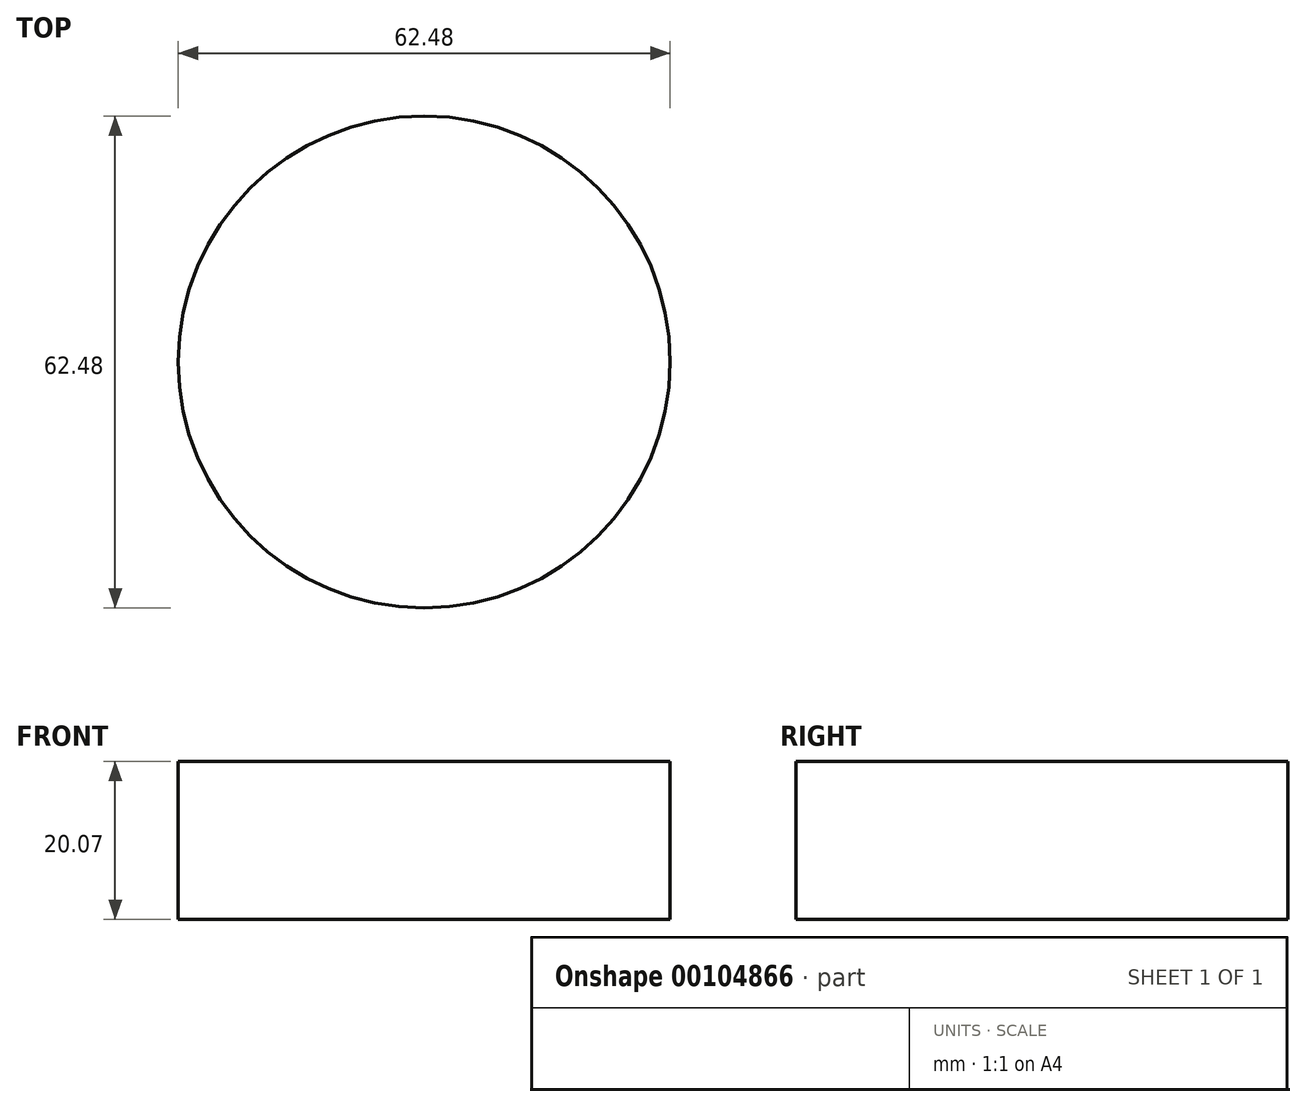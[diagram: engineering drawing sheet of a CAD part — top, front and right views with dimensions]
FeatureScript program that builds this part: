
annotation { "Feature Type Name" : "Feature", "Feature Type Description" : "" }
export const myFeature = defineFeature(function(context is Context, id is Id, definition is map)
    precondition{}
    {
        {
            var Q0;
            Q0=qCreatedBy(makeId("Top.planeOp"),FACE);
            var sketch = newSketch(context, id + "F0", { "sketchPlane" : qUnion([Q0])});
            skCircle(sketch, "E0", {"center": v(0, 0) * mm, "radius": 31.24 * mm});
            skCircle(sketch, "E1", {"center": v(0, 0) * mm, "radius": 21.46 * mm});
            skSolve(sketch);
        }
        {
            var Q0;
            Q0=makeQuery(id+"F0.imprint","IMPRINT",FACE,{"disambiguationData":[TD([[makeQuery(id+"F0.imprint","IMPRINT",EDGE,{"derivedFrom":sQuery(id+"F0.wireOp",EDGE,"E1")}),1.0]])]});
            var Q1;
            Q1=makeQuery(id+"F0.imprint","IMPRINT",FACE,{"disambiguationData":[TD([[makeQuery(id+"F0.imprint","IMPRINT",EDGE,{"derivedFrom":sQuery(id+"F0.wireOp",EDGE,"E0")}),1.0]])]});
            extrude(context, id + "F1", {"entities" : qUnion([Q0, Q1]), "depth" : 20.07 * mm});
        }
    });
